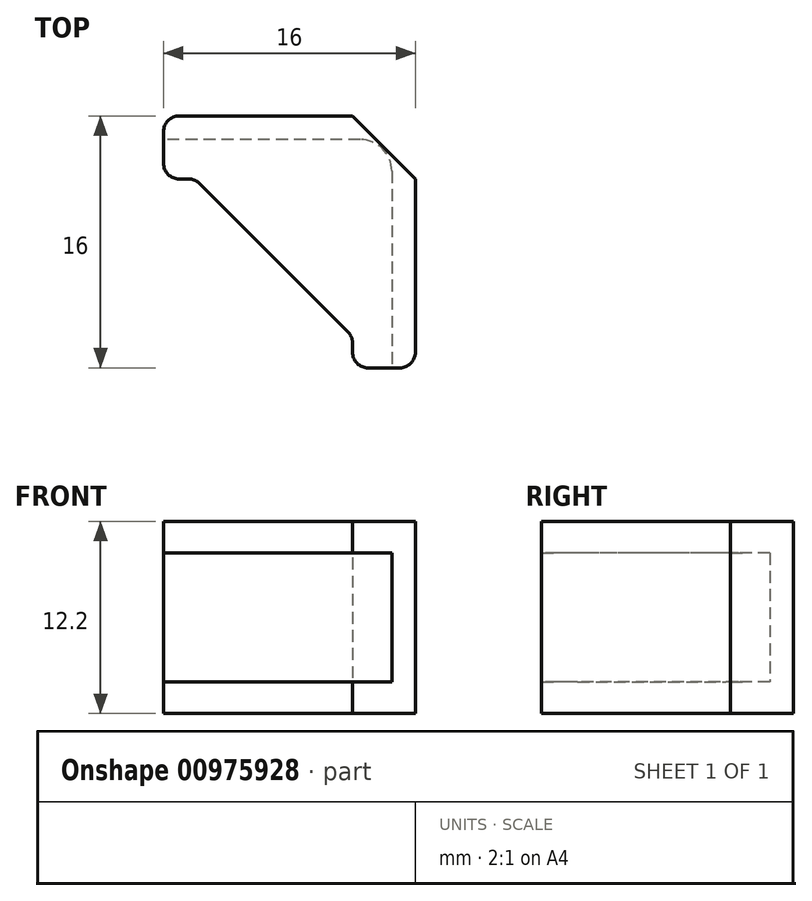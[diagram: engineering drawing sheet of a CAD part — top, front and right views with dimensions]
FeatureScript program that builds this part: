
annotation { "Feature Type Name" : "Feature", "Feature Type Description" : "" }
export const myFeature = defineFeature(function(context is Context, id is Id, definition is map)
    precondition{}
    {
        {
            var Q0;
            Q0=qCreatedBy(makeId("Top.planeOp"),FACE);
            var sketch = newSketch(context, id + "F0", { "sketchPlane" : qUnion([Q0])});
            skLineSegment(sketch, "E0.bottom", {"start": v(-45.98, 31.8) * mm, "end": v(-29.98, 31.8) * mm});
            skLineSegment(sketch, "E0.top", {"start": v(-45.98, 27.8) * mm, "end": v(-29.98, 27.8) * mm});
            skLineSegment(sketch, "E0.left", {"start": v(-45.98, 31.8) * mm, "end": v(-45.98, 27.8) * mm});
            skLineSegment(sketch, "E0.right", {"start": v(-29.98, 31.8) * mm, "end": v(-29.98, 27.8) * mm});
            skLineSegment(sketch, "E1.bottom", {"start": v(-29.98, 27.8) * mm, "end": v(-33.98, 27.8) * mm});
            skLineSegment(sketch, "E1.top", {"start": v(-29.98, 15.8) * mm, "end": v(-33.98, 15.8) * mm});
            skLineSegment(sketch, "E1.left", {"start": v(-29.98, 27.8) * mm, "end": v(-29.98, 15.8) * mm});
            skLineSegment(sketch, "E1.right", {"start": v(-33.98, 27.8) * mm, "end": v(-33.98, 15.8) * mm});
            skSolve(sketch);
        }
        {
            var Q0;
            Q0 = qSketchRegion(id + "F0", true);
            extrude(context, id + "F1", {"entities" : qUnion([Q0]), "depth" : 12.2 * mm, "offsetDistance" : 25 * mm});
        }
        {
            var Q0;
            Q0=makeQuery(id+"F1.opExtrude","SWEPT_FACE",FACE,{"disambiguationData":[OSD([sQuery(id+"F0.wireOp",EDGE,"E0.left")])]});
            var sketch = newSketch(context, id + "F2", { "sketchPlane" : qUnion([Q0])});
            skLineSegment(sketch, "E2.bottom", {"start": v(-30.3, 10.2) * mm, "end": v(-27.8, 10.2) * mm});
            skLineSegment(sketch, "E2.top", {"start": v(-30.3, 2) * mm, "end": v(-27.8, 2) * mm});
            skLineSegment(sketch, "E2.left", {"start": v(-30.3, 10.2) * mm, "end": v(-30.3, 2) * mm});
            skLineSegment(sketch, "E2.right", {"start": v(-27.8, 10.2) * mm, "end": v(-27.8, 2) * mm});
            skSolve(sketch);
        }
        {
            var Q0;
            Q0 = qSketchRegion(id + "F2", true);
            extrude(context, id + "F3", {"entities" : qUnion([Q0]), "operationType" : NewBodyOperationType.REMOVE, "oppositeDirection" : true, "depth" : 14.5 * mm, "offsetDistance" : 25 * mm});
        }
        {
            var Q0;
            Q0=makeQuery(id+"F1.opExtrude","SWEPT_FACE",FACE,{"disambiguationData":[OSD([sQuery(id+"F0.wireOp",EDGE,"E1.top")])]});
            var sketch = newSketch(context, id + "F4", { "sketchPlane" : qUnion([Q0])});
            skLineSegment(sketch, "E3.bottom", {"start": v(-31.48, 10.2) * mm, "end": v(-33.98, 10.2) * mm});
            skLineSegment(sketch, "E3.top", {"start": v(-31.48, 2) * mm, "end": v(-33.98, 2) * mm});
            skLineSegment(sketch, "E3.left", {"start": v(-31.48, 10.2) * mm, "end": v(-31.48, 2) * mm});
            skLineSegment(sketch, "E3.right", {"start": v(-33.98, 10.2) * mm, "end": v(-33.98, 2) * mm});
            skSolve(sketch);
        }
        {
            var Q0;
            Q0 = qSketchRegion(id + "F4", true);
            extrude(context, id + "F5", {"entities" : qUnion([Q0]), "operationType" : NewBodyOperationType.REMOVE, "oppositeDirection" : true, "depth" : 13.2 * mm, "offsetDistance" : 25 * mm});
        }
        {
            var Q0;
            {var subQ0=sQuery(id+"F0.wireOp",EDGE,"E0.top");var subQ1=makeQuery(id+"F1.opExtrude","SWEPT_FACE",FACE,{"disambiguationData":[OSD([subQ0])]});var subQ2=sQuery(id+"F0.wireOp",EDGE,"E1.right");var subQ3=makeQuery(id+"F1.opExtrude","SWEPT_FACE",FACE,{"disambiguationData":[OSD([subQ2])]});Q0=makeQuery(id+"F3.boolean.opBoolean","SPLIT",EDGE,{"disambiguationData":[topologyDisambiguationEdgeConnected([subQ1,subQ3]),TD([makeQuery(id+"F3.opExtrude","SWEPT_FACE",FACE,{"disambiguationData":[OSD([sQuery(id+"F2.wireOp",EDGE,"E2.bottom")])]})])],"derivedFrom":makeQuery(id+"F1.opExtrude","SWEPT_EDGE",EDGE,{"disambiguationData":[OSD([subQ0,sQuery(id+"F0.wireOp",EDGE,"E1.bottom"),subQ2])]})});}
            var Q1;
            {var subQ0=sQuery(id+"F0.wireOp",EDGE,"E1.right");var subQ1=makeQuery(id+"F1.opExtrude","SWEPT_FACE",FACE,{"disambiguationData":[OSD([subQ0])]});var subQ2=sQuery(id+"F0.wireOp",EDGE,"E0.top");var subQ3=makeQuery(id+"F1.opExtrude","SWEPT_FACE",FACE,{"disambiguationData":[OSD([subQ2])]});Q1=makeQuery(id+"F3.boolean.opBoolean","SPLIT",EDGE,{"disambiguationData":[topologyDisambiguationEdgeConnected([subQ3,subQ1]),TD([makeQuery(id+"F3.opExtrude","SWEPT_FACE",FACE,{"disambiguationData":[OSD([sQuery(id+"F2.wireOp",EDGE,"E2.top")])]})])],"derivedFrom":makeQuery(id+"F1.opExtrude","SWEPT_EDGE",EDGE,{"disambiguationData":[OSD([subQ2,sQuery(id+"F0.wireOp",EDGE,"E1.bottom"),subQ0])]})});}
            chamfer(context, id + "F6", {"entities" : qUnion([Q0, Q1]), "width" : 10 * mm, "tangentPropagation" : true});
        }
        {
            var Q0;
            Q0=makeQuery(id+"F3.boolean.opBoolean","COPY",EDGE,{"derivedFrom":makeQuery(id+"F3.opExtrude","CAP_EDGE",EDGE,{"disambiguationData":[OSD([sQuery(id+"F2.wireOp",EDGE,"E2.left")])],"isStart":false})});
            fillet(context, id + "F7", {"entities" : qUnion([Q0]), "radius" : 2 * mm, "tangentPropagation" : true, "allowEdgeOverflow" : false});
        }
        {
            var Q0;
            Q0=makeQuery(id+"F1.opExtrude","SWEPT_EDGE",EDGE,{"disambiguationData":[OSD([sQuery(id+"F0.wireOp",EDGE,"E0.bottom"),sQuery(id+"F0.wireOp",EDGE,"E0.right")])]});
            chamfer(context, id + "F8", {"entities" : qUnion([Q0]), "width" : 4 * mm, "tangentPropagation" : true});
        }
        {
            var Q0;
            {var subQ0=sQuery(id+"F0.wireOp",EDGE,"E0.left");var subQ1=sQuery(id+"F0.wireOp",EDGE,"E0.top");Q0=makeQuery(id+"F3.boolean.opBoolean","SPLIT",EDGE,{"disambiguationData":[TD([makeQuery(id+"F3.opExtrude","SWEPT_FACE",FACE,{"disambiguationData":[OSD([sQuery(id+"F2.wireOp",EDGE,"E2.bottom")])]})])],"derivedFrom":makeQuery(id+"F1.opExtrude","SWEPT_EDGE",EDGE,{"disambiguationData":[OSD([subQ1,subQ0])]})});}
            var Q1;
            {var subQ0=makeQuery(id+"F3.opExtrude","SWEPT_FACE",FACE,{"disambiguationData":[OSD([sQuery(id+"F2.wireOp",EDGE,"E2.bottom")])]});var subQ2=sQuery(id+"F0.wireOp",EDGE,"E1.right");var subQ3=makeQuery(id+"F1.opExtrude","SWEPT_FACE",FACE,{"disambiguationData":[OSD([subQ2])]});var subQ4=sQuery(id+"F0.wireOp",EDGE,"E0.top");var subQ7=makeQuery(id+"F1.opExtrude","SWEPT_FACE",FACE,{"disambiguationData":[OSD([subQ4])]});Q1=makeQuery(id+"F6.opChamfer","BLEND_EDGE",EDGE,{"blendedFrom":[makeQuery(id+"F3.boolean.opBoolean","SPLIT",EDGE,{"disambiguationData":[topologyDisambiguationEdgeConnected([subQ7,subQ3]),TD([subQ0])],"derivedFrom":makeQuery(id+"F1.opExtrude","SWEPT_EDGE",EDGE,{"disambiguationData":[OSD([subQ4,sQuery(id+"F0.wireOp",EDGE,"E1.bottom"),subQ2])]})}),makeQuery(id+"F3.boolean.opBoolean","SPLIT",FACE,{"disambiguationData":[TD([subQ0])],"derivedFrom":subQ7})],"blendedInto":[makeQuery(id+"F3.boolean.opBoolean","SPLIT",FACE,{"disambiguationData":[TD([subQ0])],"derivedFrom":subQ7})]});}
            var Q2;
            {var subQ0=makeQuery(id+"F3.opExtrude","SWEPT_FACE",FACE,{"disambiguationData":[OSD([sQuery(id+"F2.wireOp",EDGE,"E2.bottom")])]});var subQ2=sQuery(id+"F0.wireOp",EDGE,"E0.top");var subQ3=makeQuery(id+"F1.opExtrude","SWEPT_FACE",FACE,{"disambiguationData":[OSD([subQ2])]});var subQ4=sQuery(id+"F0.wireOp",EDGE,"E1.right");var subQ6=makeQuery(id+"F1.opExtrude","SWEPT_FACE",FACE,{"disambiguationData":[OSD([subQ4])]});Q2=makeQuery(id+"F6.opChamfer","BLEND_EDGE",EDGE,{"blendedFrom":[makeQuery(id+"F3.boolean.opBoolean","SPLIT",EDGE,{"disambiguationData":[topologyDisambiguationEdgeConnected([subQ3,subQ6]),TD([subQ0])],"derivedFrom":makeQuery(id+"F1.opExtrude","SWEPT_EDGE",EDGE,{"disambiguationData":[OSD([subQ2,sQuery(id+"F0.wireOp",EDGE,"E1.bottom"),subQ4])]})}),makeQuery(id+"F5.boolean.opBoolean","SPLIT",FACE,{"disambiguationData":[TD([makeQuery(id+"F3.boolean.opBoolean","COPY",FACE,{"derivedFrom":subQ0})])],"derivedFrom":subQ6})],"blendedInto":[makeQuery(id+"F5.boolean.opBoolean","SPLIT",FACE,{"disambiguationData":[TD([makeQuery(id+"F3.boolean.opBoolean","COPY",FACE,{"derivedFrom":subQ0})])],"derivedFrom":subQ6})]});}
            var Q3;
            {var subQ0=sQuery(id+"F0.wireOp",EDGE,"E1.top");var subQ1=sQuery(id+"F0.wireOp",EDGE,"E1.right");Q3=makeQuery(id+"F5.boolean.opBoolean","SPLIT",EDGE,{"disambiguationData":[TD([makeQuery(id+"F3.boolean.opBoolean","COPY",FACE,{"derivedFrom":makeQuery(id+"F3.opExtrude","SWEPT_FACE",FACE,{"disambiguationData":[OSD([sQuery(id+"F2.wireOp",EDGE,"E2.bottom")])]})})])],"derivedFrom":makeQuery(id+"F1.opExtrude","SWEPT_EDGE",EDGE,{"disambiguationData":[OSD([subQ0,subQ1])]})});}
            var Q4;
            Q4=makeQuery(id+"F1.opExtrude","SWEPT_EDGE",EDGE,{"disambiguationData":[OSD([sQuery(id+"F0.wireOp",EDGE,"E1.top"),sQuery(id+"F0.wireOp",EDGE,"E1.left")])]});
            var Q5;
            {var subQ0=sQuery(id+"F0.wireOp",EDGE,"E1.right");var subQ1=sQuery(id+"F0.wireOp",EDGE,"E1.top");Q5=makeQuery(id+"F5.boolean.opBoolean","SPLIT",EDGE,{"disambiguationData":[TD([makeQuery(id+"F3.boolean.opBoolean","COPY",FACE,{"derivedFrom":makeQuery(id+"F3.opExtrude","SWEPT_FACE",FACE,{"disambiguationData":[OSD([sQuery(id+"F2.wireOp",EDGE,"E2.top")])]})})])],"derivedFrom":makeQuery(id+"F1.opExtrude","SWEPT_EDGE",EDGE,{"disambiguationData":[OSD([subQ1,subQ0])]})});}
            var Q6;
            {var subQ0=makeQuery(id+"F3.opExtrude","SWEPT_FACE",FACE,{"disambiguationData":[OSD([sQuery(id+"F2.wireOp",EDGE,"E2.top")])]});var subQ1=sQuery(id+"F0.wireOp",EDGE,"E0.top");var subQ2=makeQuery(id+"F1.opExtrude","SWEPT_FACE",FACE,{"disambiguationData":[OSD([subQ1])]});var subQ4=sQuery(id+"F0.wireOp",EDGE,"E1.right");var subQ6=makeQuery(id+"F1.opExtrude","SWEPT_FACE",FACE,{"disambiguationData":[OSD([subQ4])]});Q6=makeQuery(id+"F6.opChamfer","BLEND_EDGE",EDGE,{"blendedFrom":[makeQuery(id+"F3.boolean.opBoolean","SPLIT",EDGE,{"disambiguationData":[topologyDisambiguationEdgeConnected([subQ2,subQ6]),TD([subQ0])],"derivedFrom":makeQuery(id+"F1.opExtrude","SWEPT_EDGE",EDGE,{"disambiguationData":[OSD([subQ1,sQuery(id+"F0.wireOp",EDGE,"E1.bottom"),subQ4])]})}),makeQuery(id+"F5.boolean.opBoolean","SPLIT",FACE,{"disambiguationData":[TD([makeQuery(id+"F3.boolean.opBoolean","COPY",FACE,{"derivedFrom":subQ0})])],"derivedFrom":subQ6})],"blendedInto":[makeQuery(id+"F5.boolean.opBoolean","SPLIT",FACE,{"disambiguationData":[TD([makeQuery(id+"F3.boolean.opBoolean","COPY",FACE,{"derivedFrom":subQ0})])],"derivedFrom":subQ6})]});}
            var Q7;
            {var subQ0=makeQuery(id+"F3.opExtrude","SWEPT_FACE",FACE,{"disambiguationData":[OSD([sQuery(id+"F2.wireOp",EDGE,"E2.top")])]});var subQ1=sQuery(id+"F0.wireOp",EDGE,"E1.right");var subQ2=makeQuery(id+"F1.opExtrude","SWEPT_FACE",FACE,{"disambiguationData":[OSD([subQ1])]});var subQ4=sQuery(id+"F0.wireOp",EDGE,"E0.top");var subQ7=makeQuery(id+"F1.opExtrude","SWEPT_FACE",FACE,{"disambiguationData":[OSD([subQ4])]});Q7=makeQuery(id+"F6.opChamfer","BLEND_EDGE",EDGE,{"blendedFrom":[makeQuery(id+"F3.boolean.opBoolean","SPLIT",EDGE,{"disambiguationData":[topologyDisambiguationEdgeConnected([subQ7,subQ2]),TD([subQ0])],"derivedFrom":makeQuery(id+"F1.opExtrude","SWEPT_EDGE",EDGE,{"disambiguationData":[OSD([subQ4,sQuery(id+"F0.wireOp",EDGE,"E1.bottom"),subQ1])]})}),makeQuery(id+"F3.boolean.opBoolean","SPLIT",FACE,{"disambiguationData":[TD([subQ0])],"derivedFrom":subQ7})],"blendedInto":[makeQuery(id+"F3.boolean.opBoolean","SPLIT",FACE,{"disambiguationData":[TD([subQ0])],"derivedFrom":subQ7})]});}
            var Q8;
            {var subQ0=sQuery(id+"F0.wireOp",EDGE,"E0.left");var subQ1=sQuery(id+"F0.wireOp",EDGE,"E0.top");Q8=makeQuery(id+"F3.boolean.opBoolean","SPLIT",EDGE,{"disambiguationData":[TD([makeQuery(id+"F3.opExtrude","SWEPT_FACE",FACE,{"disambiguationData":[OSD([sQuery(id+"F2.wireOp",EDGE,"E2.top")])]})])],"derivedFrom":makeQuery(id+"F1.opExtrude","SWEPT_EDGE",EDGE,{"disambiguationData":[OSD([subQ1,subQ0])]})});}
            var Q9;
            Q9=makeQuery(id+"F1.opExtrude","SWEPT_EDGE",EDGE,{"disambiguationData":[OSD([sQuery(id+"F0.wireOp",EDGE,"E0.bottom"),sQuery(id+"F0.wireOp",EDGE,"E0.left")])]});
            fillet(context, id + "F9", {"entities" : qUnion([Q0, Q1, Q2, Q3, Q4, Q5, Q6, Q7, Q8, Q9]), "radius" : 1 * mm, "tangentPropagation" : true, "allowEdgeOverflow" : false});
        }
    });
